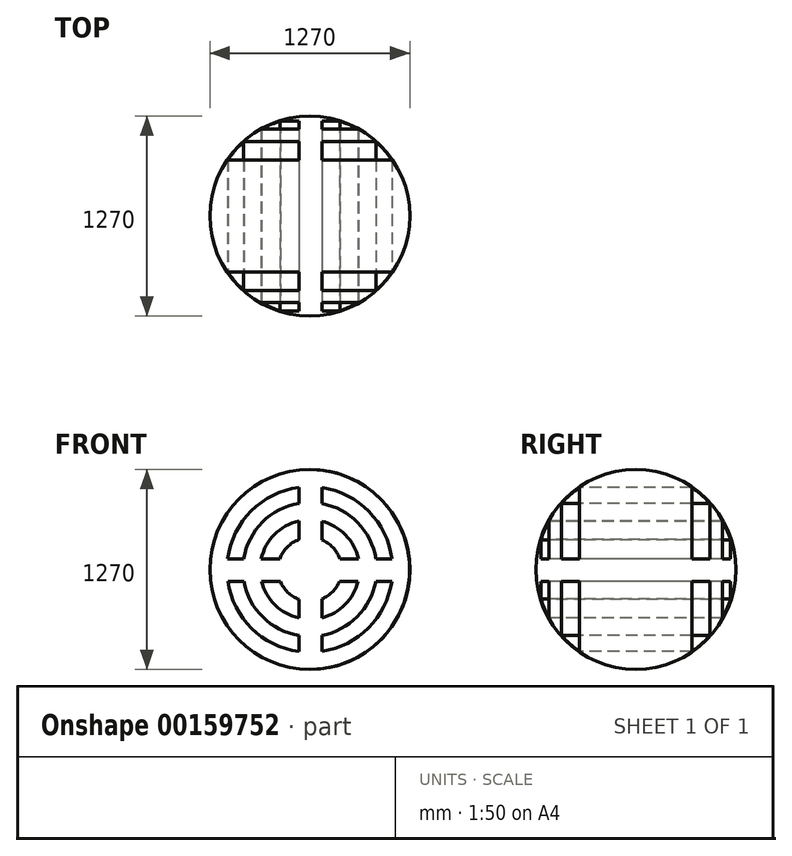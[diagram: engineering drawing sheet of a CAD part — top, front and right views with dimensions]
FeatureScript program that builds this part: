
annotation { "Feature Type Name" : "Feature", "Feature Type Description" : "" }
export const myFeature = defineFeature(function(context is Context, id is Id, definition is map)
    precondition{}
    {
        {
            var Q0;
            Q0=qCreatedBy(makeId("Front.planeOp"),FACE);
            var sketch = newSketch(context, id + "F0", { "sketchPlane" : qUnion([Q0])});
            skArc(sketch, "E0", {"start": v(0, 635) * mm, "mid": v(-635, 0) * mm, "end": v(0, -635) * mm});
            skLineSegment(sketch, "E1", {"start": v(0, 635) * mm, "end": v(0, -635) * mm});
            skSolve(sketch);
        }
        {
            var Q0;
            Q0=makeQuery(id+"F0.imprint","IMPRINT",FACE,{"disambiguationData":[TD([[makeQuery(id+"F0.imprint","IMPRINT",EDGE,{"derivedFrom":sQuery(id+"F0.wireOp",EDGE,"E0")}),1.0]])]});
            var Q1;
            Q1=sQuery(id+"F0.wireOp",EDGE,"E1");
            revolve(context, id + "F1", {"entities" : qUnion([Q0]), "axis" : qUnion([Q1]), "revolveType" : RevolveType.FULL});
        }
        {
            var Q0;
            Q0=qCreatedBy(makeId("Front.planeOp"),FACE);
            var sketch = newSketch(context, id + "F2", { "sketchPlane" : qUnion([Q0])});
            skLineSegment(sketch, "E2", {"start": v(0, 684.29) * mm, "end": v(0, -736.15) * mm, "construction": true});
            skLineSegment(sketch, "E3", {"start": v(-697.8, 0) * mm, "end": v(666.05, 0) * mm});
            skLineSegment(sketch, "E4", {"start": v(-68.8, 521.03) * mm, "end": v(-68.8, 419.64) * mm});
            skLineSegment(sketch, "E5", {"start": v(75.9, 520.04) * mm, "end": v(75.9, 418.41) * mm});
            skLineSegment(sketch, "E6", {"start": v(-521.14, 67.94) * mm, "end": v(-419.78, 67.94) * mm});
            skLineSegment(sketch, "E7", {"start": v(520.24, -74.53) * mm, "end": v(418.66, -74.53) * mm});
            skArc(sketch, "E8", {"start": v(-68.8, 521.03) * mm, "mid": v(-371.92, 371.32) * mm, "end": v(-521.14, 67.94) * mm});
            skArc(sketch, "E9", {"start": v(-68.8, 419.64) * mm, "mid": v(-301, 300.39) * mm, "end": v(-419.78, 67.94) * mm});
            skArc(sketch, "E10", {"start": v(-68.8, 308.28) * mm, "mid": v(-223.66, 223.04) * mm, "end": v(-308.47, 67.94) * mm});
            skArc(sketch, "E11", {"start": v(-68.8, 189.96) * mm, "mid": v(-143.18, 142.54) * mm, "end": v(-190.27, 67.94) * mm});
            skLineSegment(sketch, "E12.trimOffspring", {"start": v(-68.8, 308.28) * mm, "end": v(-68.8, 189.96) * mm});
            skLineSegment(sketch, "E13.trimOffspring", {"start": v(75.9, -187.23) * mm, "end": v(75.9, -306.6) * mm});
            skLineSegment(sketch, "E14.trimOffspring", {"start": v(75.9, 306.6) * mm, "end": v(75.9, 187.23) * mm});
            skLineSegment(sketch, "E15.trimOffspring", {"start": v(419.78, 67.94) * mm, "end": v(521.14, 67.94) * mm});
            skLineSegment(sketch, "E16.trimOffspring", {"start": v(306.94, -74.53) * mm, "end": v(187.78, -74.53) * mm});
            skLineSegment(sketch, "E17.trimOffspring", {"start": v(75.9, -418.41) * mm, "end": v(75.9, -520.04) * mm});
            skLineSegment(sketch, "E18.trimOffspring", {"start": v(-68.8, -419.64) * mm, "end": v(-68.8, -521.03) * mm});
            skLineSegment(sketch, "E19.trimOffspring", {"start": v(-418.66, -74.53) * mm, "end": v(-520.24, -74.53) * mm});
            skLineSegment(sketch, "E20.trimOffspring", {"start": v(-308.47, 67.94) * mm, "end": v(-190.27, 67.94) * mm});
            skArc(sketch, "E21.trimOffspring", {"start": v(-520.24, -74.53) * mm, "mid": v(-369.57, -373.67) * mm, "end": v(-68.8, -521.03) * mm});
            skArc(sketch, "E22.trimOffspring", {"start": v(-418.66, -74.53) * mm, "mid": v(-298.62, -302.74) * mm, "end": v(-68.8, -419.64) * mm});
            skArc(sketch, "E23.trimOffspring", {"start": v(-306.94, -74.53) * mm, "mid": v(-221.25, -225.42) * mm, "end": v(-68.8, -308.28) * mm});
            skArc(sketch, "E24.trimOffspring", {"start": v(-187.78, -74.53) * mm, "mid": v(-140.67, -145.01) * mm, "end": v(-68.8, -189.96) * mm});
            skArc(sketch, "E25.trimOffspring", {"start": v(190.27, 67.94) * mm, "mid": v(145.84, 139.82) * mm, "end": v(75.9, 187.23) * mm});
            skArc(sketch, "E26.trimOffspring", {"start": v(308.47, 67.94) * mm, "mid": v(226.22, 220.44) * mm, "end": v(75.9, 306.6) * mm});
            skArc(sketch, "E27.trimOffspring", {"start": v(419.78, 67.94) * mm, "mid": v(303.53, 297.82) * mm, "end": v(75.9, 418.41) * mm});
            skArc(sketch, "E28.trimOffspring", {"start": v(521.14, 67.94) * mm, "mid": v(374.45, 368.77) * mm, "end": v(75.9, 520.04) * mm});
            skArc(sketch, "E29.trimOffspring", {"start": v(75.9, -306.6) * mm, "mid": v(223.85, -222.85) * mm, "end": v(306.94, -74.53) * mm});
            skArc(sketch, "E30.trimOffspring", {"start": v(75.9, -187.23) * mm, "mid": v(143.38, -142.34) * mm, "end": v(187.78, -74.53) * mm});
            skArc(sketch, "E31.trimOffspring", {"start": v(75.9, -418.41) * mm, "mid": v(301.18, -300.2) * mm, "end": v(418.66, -74.53) * mm});
            skArc(sketch, "E32.trimOffspring", {"start": v(75.9, -520.04) * mm, "mid": v(372.11, -371.13) * mm, "end": v(520.24, -74.53) * mm});
            skLineSegment(sketch, "E33.trimOffspring", {"start": v(-68.8, -189.96) * mm, "end": v(-68.8, -308.28) * mm});
            skLineSegment(sketch, "E34.trimOffspring", {"start": v(190.27, 67.94) * mm, "end": v(308.47, 67.94) * mm});
            skLineSegment(sketch, "E35.trimOffspring", {"start": v(-187.78, -74.53) * mm, "end": v(-306.94, -74.53) * mm});
            skSolve(sketch);
        }
        {
            var Q0;
            Q0 = qSketchRegion(id + "F2", true);
            extrude(context, id + "F3", {"entities" : qUnion([Q0]), "operationType" : NewBodyOperationType.REMOVE, "endBound" : BoundingType.THROUGH_ALL, "oppositeDirection" : true, "depth" : 60 * mm, "hasSecondDirection" : true, "secondDirectionBound" : SecondDirectionBoundingType.THROUGH_ALL, "secondDirectionOppositeDirection" : false, "secondDirectionDepth" : 25.4 * mm});
        }
    });
